# Revit family: QF_Brema_VM500W_WM900W_cat
name_source: partatom
category: Specialty Equipment
revit_build: Autodesk Revit MEP 2012 (Build: 20110916_2132(x64)
units: mm (PartAtom-declared; Revit-internal decimal feet)

## types (2) — shared parameters
Assembly Code = E1090320
BTUH = 0 W
Cold Water Connection Height = 252 mm  [stored 0.826772 ft]
Cold Water Maximum Pressure = 6.0 bar
Cold Water Minimum Pressure = 1.0 bar
Cold Water Size = 1"
Cold Water Size Radius = 1/2"
Conn Conduit = Yes
Cycle = 50 Hz
Depth = 550 mm
Description = AUTOMATIC ICE CUBE MAKER WATER COOLED
Elec Conn Connection Height = 323 mm
FL Amps = 0 A
Height = 805 mm  [stored 2.64108 ft]
Indirect Waste Connection Height = 40 mm  [stored 0.131234 ft]
Indirect Waste Radius = 1/2"
Indirect Waste Size = 1"
Manufacturer = BREMA
Min Ckt Ampacity = 0 A
Phase = 1
Refrigerant Type = R404A
URL = www.bremaice.it
Volts = 230 V
Width = 770 mm  [stored 2.52625 ft]

## per-type parameters (varying)
| type | Apparent Power | Max Overcurrent Protection | Watts | Weight |
| VM500W | 1600 VA | 20 A | 1600 W | 90 kg |
| VM900W | 3000 VA | 32 A | 3000 W | 113 kg |

note: column(s) folded — value = type name in every type: Model

note: [stored X ft] marks values corroborated as IEEE doubles in the binary element streams (Revit-internal decimal feet)

## geometry (parser evidence)
native form markers: Blend x7, Sweep x1
no freeform markers — native parametric forms only
